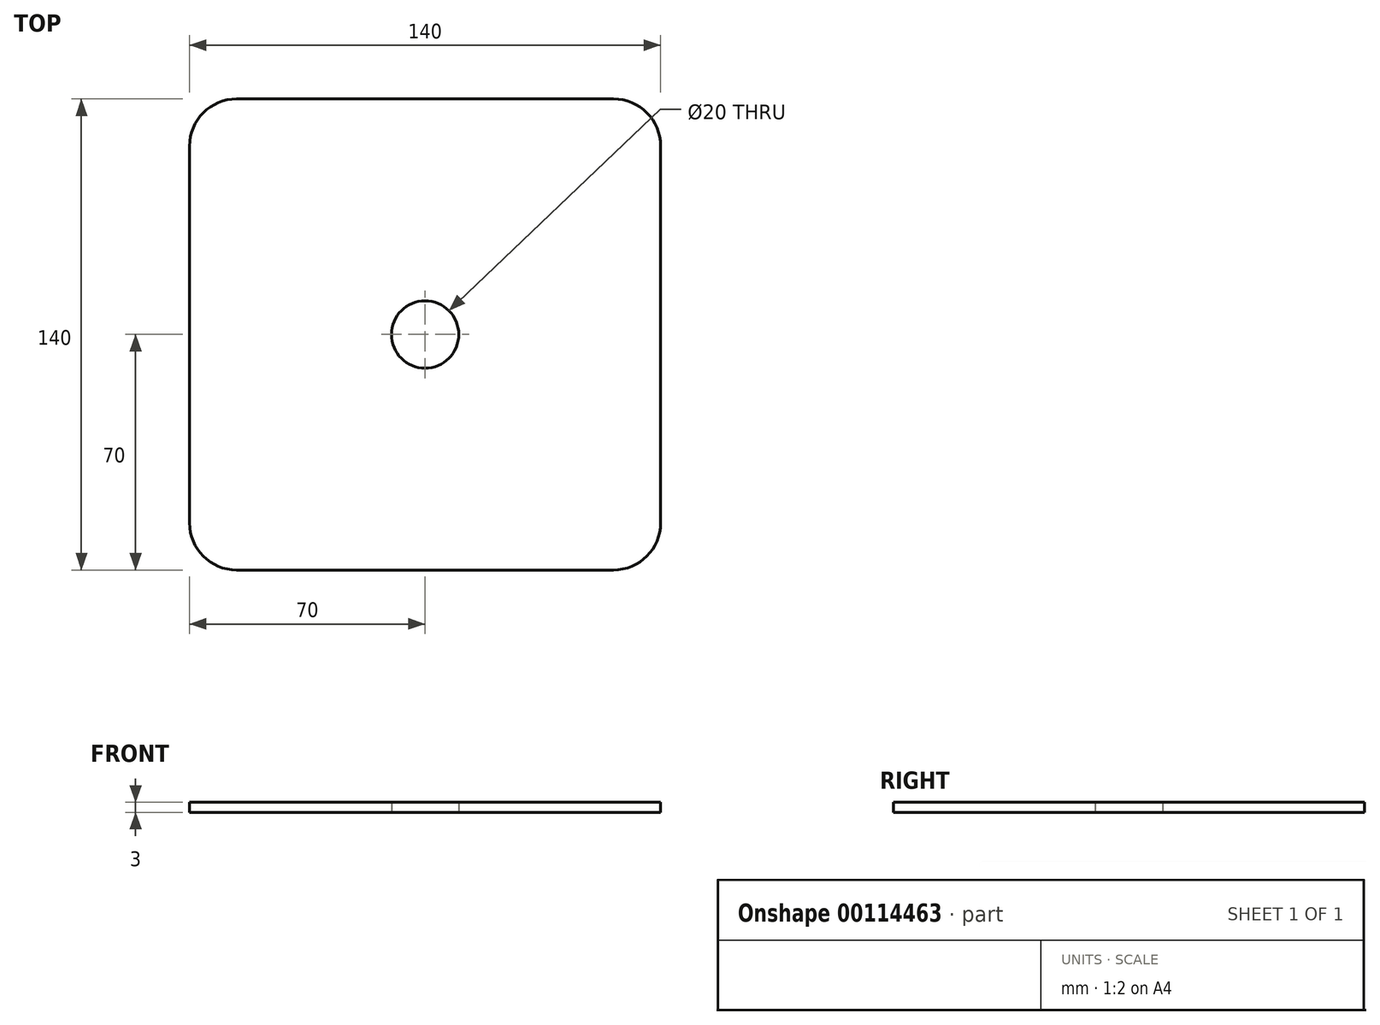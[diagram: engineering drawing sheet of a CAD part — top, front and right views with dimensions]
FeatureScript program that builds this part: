
annotation { "Feature Type Name" : "Feature", "Feature Type Description" : "" }
export const myFeature = defineFeature(function(context is Context, id is Id, definition is map)
    precondition{}
    {
        {
            var Q0;
            Q0=qCreatedBy(makeId("Top.planeOp"),FACE);
            var sketch = newSketch(context, id + "F0", { "sketchPlane" : qUnion([Q0])});
            skLineSegment(sketch, "E0.bottom", {"start": v(56, -70) * mm, "end": v(-56, -70) * mm});
            skLineSegment(sketch, "E0.top", {"start": v(56, 70) * mm, "end": v(-56, 70) * mm});
            skLineSegment(sketch, "E0.left", {"start": v(70, -56) * mm, "end": v(70, 56) * mm});
            skLineSegment(sketch, "E0.right", {"start": v(-70, -56) * mm, "end": v(-70, 56) * mm});
            skPoint(sketch, "E0.middle", {"position": v(0, 0) * mm});
            skPoint(sketch, "E1.visualSharp", {"position": v(-70, 70) * mm});
            skArc(sketch, "E1.filletArc", {"start": v(-56, 70) * mm, "mid": v(-65.9, 65.9) * mm, "end": v(-70, 56) * mm});
            skPoint(sketch, "E2.visualSharp", {"position": v(70, 70) * mm});
            skArc(sketch, "E2.filletArc", {"start": v(70, 56) * mm, "mid": v(65.9, 65.9) * mm, "end": v(56, 70) * mm});
            skPoint(sketch, "E3.visualSharp", {"position": v(70, -70) * mm});
            skArc(sketch, "E3.filletArc", {"start": v(56, -70) * mm, "mid": v(65.9, -65.9) * mm, "end": v(70, -56) * mm});
            skPoint(sketch, "E4.visualSharp", {"position": v(-70, -70) * mm});
            skArc(sketch, "E4.filletArc", {"start": v(-70, -56) * mm, "mid": v(-65.9, -65.9) * mm, "end": v(-56, -70) * mm});
            skCircle(sketch, "E5", {"center": v(0, 0) * mm, "radius": 10 * mm});
            skSolve(sketch);
        }
        {
            var Q0;
            Q0 = qSketchRegion(id + "F0", true);
            extrude(context, id + "F1", {"entities" : qUnion([Q0]), "depth" : 3 * mm});
        }
    });
